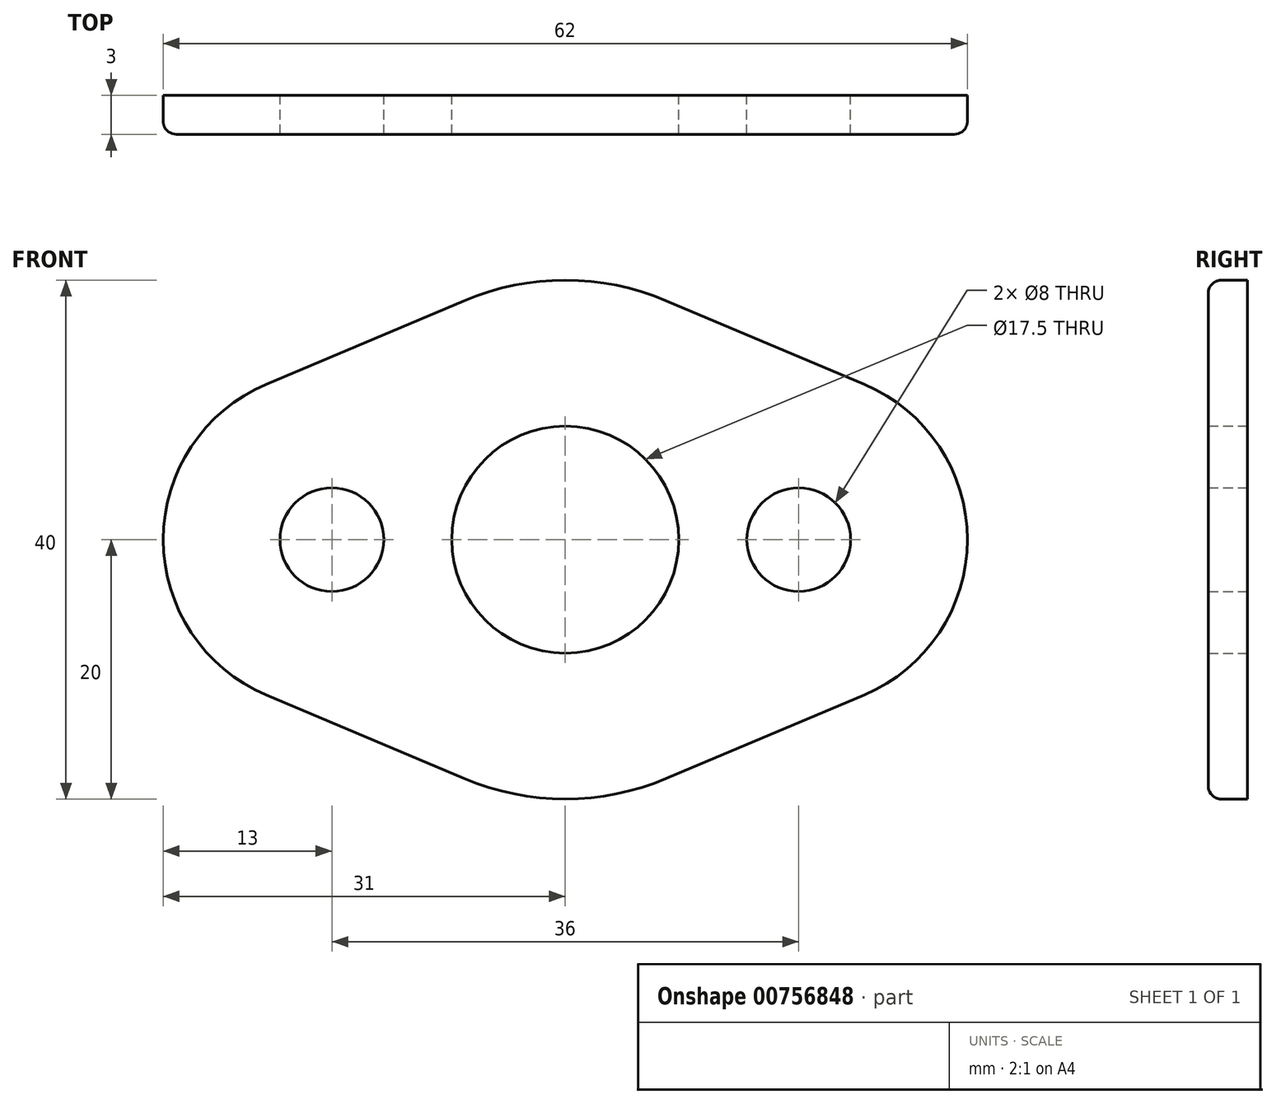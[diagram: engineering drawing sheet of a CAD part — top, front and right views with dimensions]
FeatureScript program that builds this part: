
annotation { "Feature Type Name" : "Feature", "Feature Type Description" : "" }
export const myFeature = defineFeature(function(context is Context, id is Id, definition is map)
    precondition{}
    {
        {
            var Q0;
            Q0=qCreatedBy(makeId("Front.planeOp"),FACE);
            var sketch = newSketch(context, id + "F0", { "sketchPlane" : qUnion([Q0])});
            skCircle(sketch, "E0", {"center": v(0, 0) * mm, "radius": 8.75 * mm});
            skCircle(sketch, "E1", {"center": v(-18, 0) * mm, "radius": 4 * mm});
            skCircle(sketch, "E2", {"center": v(18, 0) * mm, "radius": 4 * mm});
            skArc(sketch, "E3", {"start": v(-7.78, -18.43) * mm, "mid": v(0, -20) * mm, "end": v(7.78, -18.43) * mm});
            skArc(sketch, "E4", {"start": v(-23.06, 11.98) * mm, "mid": v(-31, 0) * mm, "end": v(-23.06, -11.98) * mm});
            skArc(sketch, "E5", {"start": v(23.06, -11.98) * mm, "mid": v(31, 0) * mm, "end": v(23.06, 11.98) * mm});
            skLineSegment(sketch, "E6", {"start": v(-23.06, 11.98) * mm, "end": v(-7.78, 18.43) * mm});
            skLineSegment(sketch, "E7", {"start": v(7.78, 18.43) * mm, "end": v(23.06, 11.98) * mm});
            skLineSegment(sketch, "E8", {"start": v(23.06, -11.98) * mm, "end": v(7.78, -18.43) * mm});
            skLineSegment(sketch, "E9", {"start": v(-7.78, -18.43) * mm, "end": v(-23.06, -11.98) * mm});
            skArc(sketch, "E10.trimOffspring", {"start": v(7.78, 18.43) * mm, "mid": v(0, 20) * mm, "end": v(-7.78, 18.43) * mm});
            skSolve(sketch);
        }
        {
            var Q0;
            Q0=makeQuery(id+"F0.imprint","IMPRINT",FACE,{"disambiguationData":[TD([[makeQuery(id+"F0.imprint","IMPRINT",EDGE,{"derivedFrom":sQuery(id+"F0.wireOp",EDGE,"E0")}),-1.0]])]});
            extrude(context, id + "F1", {"entities" : qUnion([Q0]), "depth" : 3 * mm, "offsetDistance" : 25 * mm});
        }
        {
            var Q0;
            Q0=makeQuery(id+"F1.opExtrude","CAP_EDGE",EDGE,{"disambiguationData":[OSD([sQuery(id+"F0.wireOp",EDGE,"E7")])],"isStart":false});
            fillet(context, id + "F2", {"entities" : qUnion([Q0]), "radius" : 1 * mm, "tangentPropagation" : true, "allowEdgeOverflow" : false});
        }
    });
